# Revit family: MELO CYLINDER PENDANT LIGHT
name_source: partatom
category: Lighting Fixtures
units: mm (PartAtom-declared; Revit-internal decimal feet)

## family parameters
Cut with Voids When Loaded = No
Host = Face
Light Source = Yes
Part Type = Normal
Room Calculation Point = No
Round Connector Dimension = Use Diameter
Shared = No

## types (15) — shared parameters
Apparent Load = 0 VA
Average life based on 104F(HRS) = 50000
Baffle = GOLDEN
CRI = 80
Color Filter = 16777215
Default Elevation = 0' - 0"
Description = The MELO cylinder would greatly create possibilities in the whole commercial area. Multiple sizes, beam 
options , and high visual comfort COB LED.
Dimming / Control = 0-10V
Dimming Lamp Color Temperature Shift = <None>
Finish/Color = BLACK
IP Rating = Wet Location
Load Classification = Lighting
Manufacturer = Above All Lighting
Pendant Rod Length = 4' - 0"
Power Factor = 1
Tilt Angle = -90.00°
Type Comments = MELO CYLINDER PENDANT LIGHT
URL = https://www.abovealllighting.com

## per-type parameters (varying)
| type | BEAMING ANGLE | C1 H | C2 H | Fixture Diameter | Order number | Photometric Web File | Size 04 | Size 06 | Size 08 | Wattage Comments |
| MELO04R-SP30801-10D-15-GD-BK | 15.00° | 0' - 2 19/32" | 0' - 2 5/16" | 0' - 3 29/32" | 17290 | generic | Yes | No | No | 25W/18W/12W |
| MELO04R-SP30801-10D-24-GD-BK | 24.00° | 0' - 2 19/32" | 0' - 2 5/16" | 0' - 3 29/32" | 17286 | generic | Yes | No | No | 25W/18W/12W |
| MELO04R-SP30801-10D-60-GD-BK | 60.00° | 0' - 2 19/32" | 0' - 2 5/16" | 0' - 3 29/32" | 17292 | MELO04R-SP30801-10D-60.IES | Yes | No | No | 25W/18W/12W |
| MELO04R-SP30801-10D-36-GD-BK | 36.00° | 0' - 2 19/32" | 0' - 2 5/16" | 0' - 3 29/32" | 17291 | MELO04R-SP30901-10D-36_(25W).IES | Yes | No | No | 25W/18W/12W |
| MELO04R-SP30801-10D-90-GD-BK | 90.00° | 0' - 2 19/32" | 0' - 2 5/16" | 0' - 3 29/32" | 17293 | generic | Yes | No | No | 25W/18W/12W |
| MELO06R-SP30801-10D-15-GD-BK | 15.00° | 0' - 3 1/16" | 0' - 2 27/32" | 0' - 5 13/16" | 17294 | MELO06R_SP30801_10D_15.IES | No | Yes | No | 40W/30W/20W |
| MELO06R-SP30801-10D-24-GD-BK | 24.00° | 0' - 3 1/16" | 0' - 2 27/32" | 0' - 5 13/16" | 17295 | MELO06R_SP30801_10D_24.IES | No | Yes | No | 40W/30W/20W |
| MELO06R-SP30801-10D-36-GD-BK | 36.00° | 0' - 3 1/16" | 0' - 2 27/32" | 0' - 5 13/16" | 17296 | MELO06R_SP30801_10D_36.IES | No | Yes | No | 40W/30W/20W |
| MELO06R-SP30801-10D-60-GD-BK | 60.00° | 0' - 3 1/16" | 0' - 2 27/32" | 0' - 5 13/16" | 17297 | MELO06R_SP30801_10D_60.IES | No | Yes | No | 40W/30W/20W |
| MELO06R-SP30801-10D-90-GD-BK | 90.00° | 0' - 3 1/16" | 0' - 2 27/32" | 0' - 5 13/16" | 17298 | generic.ies | No | Yes | No | 40W/30W/20W |
| MELO08R-SP30801-10D-15-GD-BK | 15.00° | 0' - 3 13/16" | 0' - 3 29/32" | 0' - 7 13/16" | 17299 | MELO08R_SP30801_10D_15.IES | No | No | Yes | 58W/44W/29W |
| MELO08R-SP30801-10D-90-GD-BK | 90.00° | 0' - 3 13/16" | 0' - 3 29/32" | 0' - 7 13/16" | 17303 | generic.ies | No | No | Yes | 58W/44W/29W |
| MELO08R-SP30801-10D-24-GD-BK | 24.00° | 0' - 3 13/16" | 0' - 3 29/32" | 0' - 7 13/16" | 17300 | MELO08R_SP30801_10D_24.IES | No | No | Yes | 58W/44W/29W |
| MELO08R-SP30801-10D-36-GD-BK | 36.00° | 0' - 3 13/16" | 0' - 3 29/32" | 0' - 7 13/16" | 17301 | MELO08R_SP30801_10D_36.IES | No | No | Yes | 58W/44W/29W |
| MELO08R-SP30801-10D-60-GD-BK | 60.00° | 0' - 3 13/16" | 0' - 3 29/32" | 0' - 7 13/16" | 17302 | MELO08R_SP30801_10D_60.IES | No | No | Yes | 58W/44W/29W |

note: column(s) folded — value = type name in every type: Model

## geometry (parser evidence)
native form markers: Sweep x10
no freeform markers — native parametric forms only
